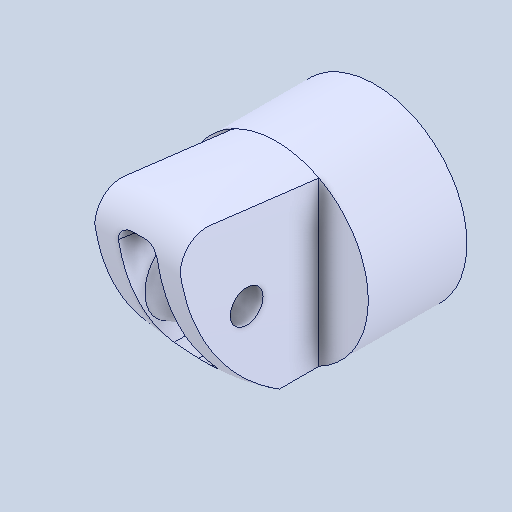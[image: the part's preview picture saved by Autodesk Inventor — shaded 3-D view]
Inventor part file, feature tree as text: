
AUTODESK INVENTOR PART (.ipt)
format: ipt  version: 2022 (Build 260153000, 153)  size: 225,792 bytes
history: mixed  units: mm
features: other x1, fillet x1, imported_body x1
ambient origin geometry x8: Origin, YZ Plane, XZ Plane, XY Plane, X Axis, Y Axis, Z Axis, Center Point
bodies: Body1 (imported_parasolid)
feature tree (3):
  other  "Sólido1"
  fillet  "Fillet1"  [1 undecoded]
  imported_body  NMx_Import_Brep_tag  [imported B-rep: ~8 faces, bbox_mm=[1.0, 0.0, 0.0]]
note: 1 required parameter value undecoded (feature->parameter linkage not recoverable at this tier; creation-order binding heuristic only, values carry confidence <= 0.55)
